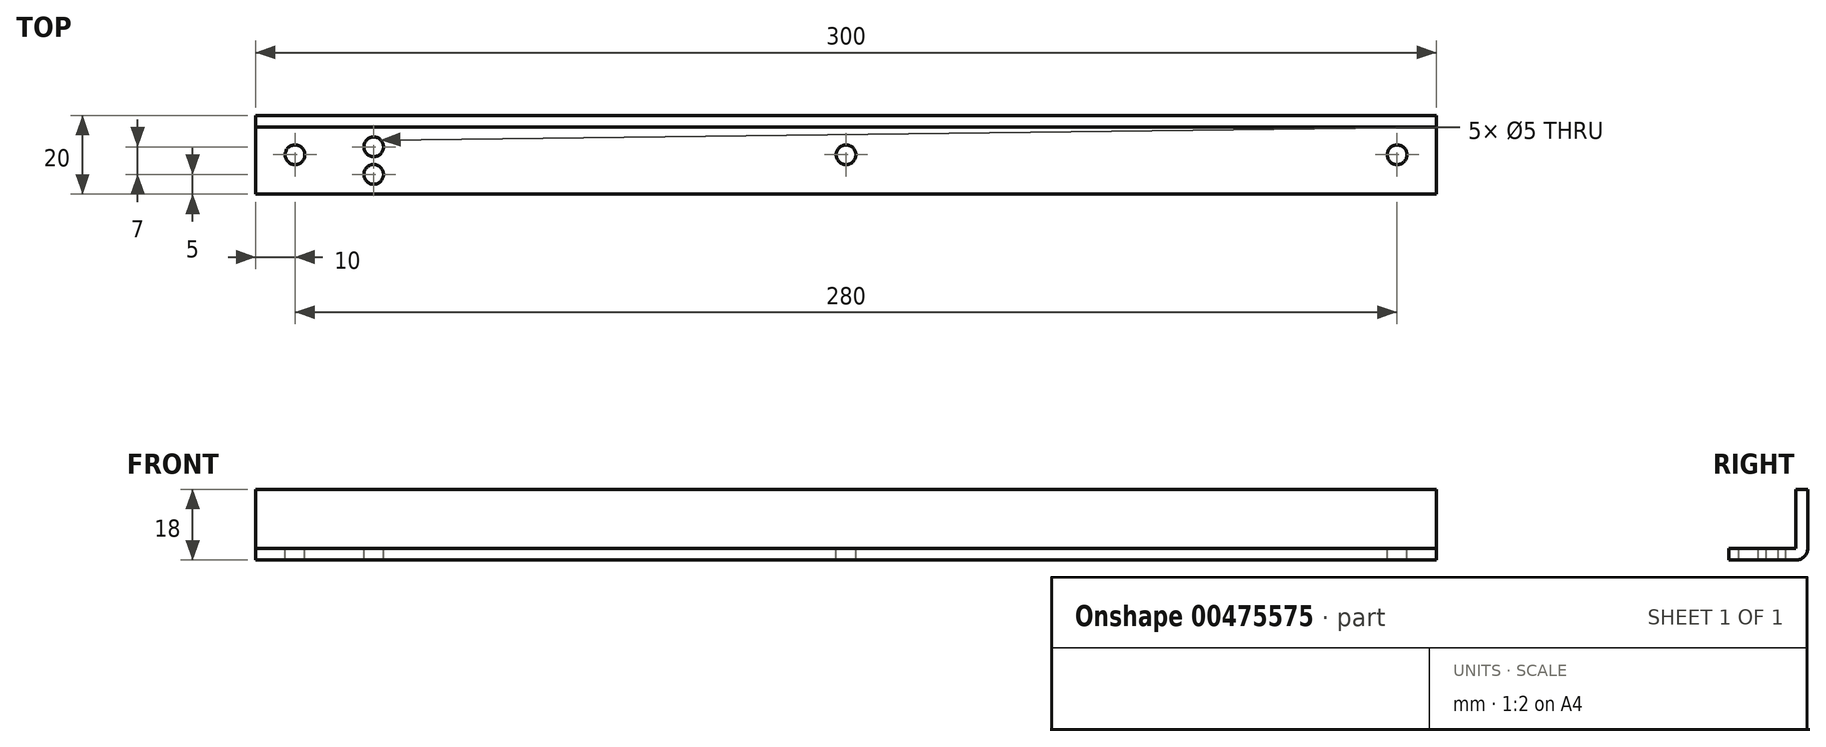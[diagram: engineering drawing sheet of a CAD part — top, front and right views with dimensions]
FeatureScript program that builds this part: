
annotation { "Feature Type Name" : "Feature", "Feature Type Description" : "" }
export const myFeature = defineFeature(function(context is Context, id is Id, definition is map)
    precondition{}
    {
        {
            var Q0;
            Q0=qCreatedBy(makeId("Top.planeOp"),FACE);
            var sketch = newSketch(context, id + "F0", { "sketchPlane" : qUnion([Q0])});
            skLineSegment(sketch, "E0.bottom", {"start": v(150, 10) * mm, "end": v(-150, 10) * mm});
            skLineSegment(sketch, "E0.top", {"start": v(150, -10) * mm, "end": v(-150, -10) * mm});
            skLineSegment(sketch, "E0.left", {"start": v(150, 10) * mm, "end": v(150, -10) * mm});
            skLineSegment(sketch, "E0.right", {"start": v(-150, 10) * mm, "end": v(-150, -10) * mm});
            skPoint(sketch, "E0.middle", {"position": v(0, 0) * mm});
            skSolve(sketch);
        }
        {
            var Q0;
            Q0 = qSketchRegion(id + "F0", true);
            extrude(context, id + "F1", {"entities" : qUnion([Q0]), "depth" : 3 * mm, "offsetDistance" : 25 * mm});
        }
        {
            var Q0;
            Q0=makeQuery(id+"F1.opExtrude","CAP_FACE",FACE,{"disambiguationData":[OSD([sQuery(id+"F0.wireOp",EDGE,"E0.bottom"),sQuery(id+"F0.wireOp",EDGE,"E0.top"),sQuery(id+"F0.wireOp",EDGE,"E0.left"),sQuery(id+"F0.wireOp",EDGE,"E0.right")])],"isStart":false});
            var sketch = newSketch(context, id + "F2", { "sketchPlane" : qUnion([Q0])});
            skCircle(sketch, "E1", {"center": v(-120, 2) * mm, "radius": 2.5 * mm});
            skCircle(sketch, "E2", {"center": v(-120, -5) * mm, "radius": 2.5 * mm});
            skCircle(sketch, "E3", {"center": v(-140, 0) * mm, "radius": 2.5 * mm});
            skCircle(sketch, "E4", {"center": v(0, 0) * mm, "radius": 2.5 * mm});
            skCircle(sketch, "E5", {"center": v(140, 0) * mm, "radius": 2.5 * mm});
            skSolve(sketch);
        }
        {
            var Q0;
            Q0 = qSketchRegion(id + "F2", true);
            extrude(context, id + "F3", {"entities" : qUnion([Q0]), "operationType" : NewBodyOperationType.REMOVE, "oppositeDirection" : true, "depth" : 3 * mm, "offsetDistance" : 25 * mm});
        }
        {
            var Q0;
            Q0=makeQuery(id+"F1.opExtrude","CAP_FACE",FACE,{"disambiguationData":[OSD([sQuery(id+"F0.wireOp",EDGE,"E0.bottom"),sQuery(id+"F0.wireOp",EDGE,"E0.top"),sQuery(id+"F0.wireOp",EDGE,"E0.left"),sQuery(id+"F0.wireOp",EDGE,"E0.right")])],"isStart":false});
            var sketch = newSketch(context, id + "F4", { "sketchPlane" : qUnion([Q0])});
            skLineSegment(sketch, "E6.bottom", {"start": v(-150, 10) * mm, "end": v(150, 10) * mm});
            skLineSegment(sketch, "E6.top", {"start": v(-150, 7) * mm, "end": v(150, 7) * mm});
            skLineSegment(sketch, "E6.left", {"start": v(-150, 10) * mm, "end": v(-150, 7) * mm});
            skLineSegment(sketch, "E6.right", {"start": v(150, 10) * mm, "end": v(150, 7) * mm});
            skSolve(sketch);
        }
        {
            var Q0;
            Q0 = qSketchRegion(id + "F4", true);
            extrude(context, id + "F5", {"entities" : qUnion([Q0]), "operationType" : NewBodyOperationType.ADD, "depth" : 15 * mm, "offsetDistance" : 25 * mm});
        }
        {
            var Q0;
            Q0=makeQuery(id+"F1.opExtrude","CAP_EDGE",EDGE,{"disambiguationData":[OSD([sQuery(id+"F0.wireOp",EDGE,"E0.bottom")])],"isStart":true});
            fillet(context, id + "F6", {"entities" : qUnion([Q0]), "tangentPropagation" : true, "radius" : 3 * mm, "defaultsChanged" : true, "vertexSettings" : [], "allowEdgeOverflow" : false});
        }
    });
